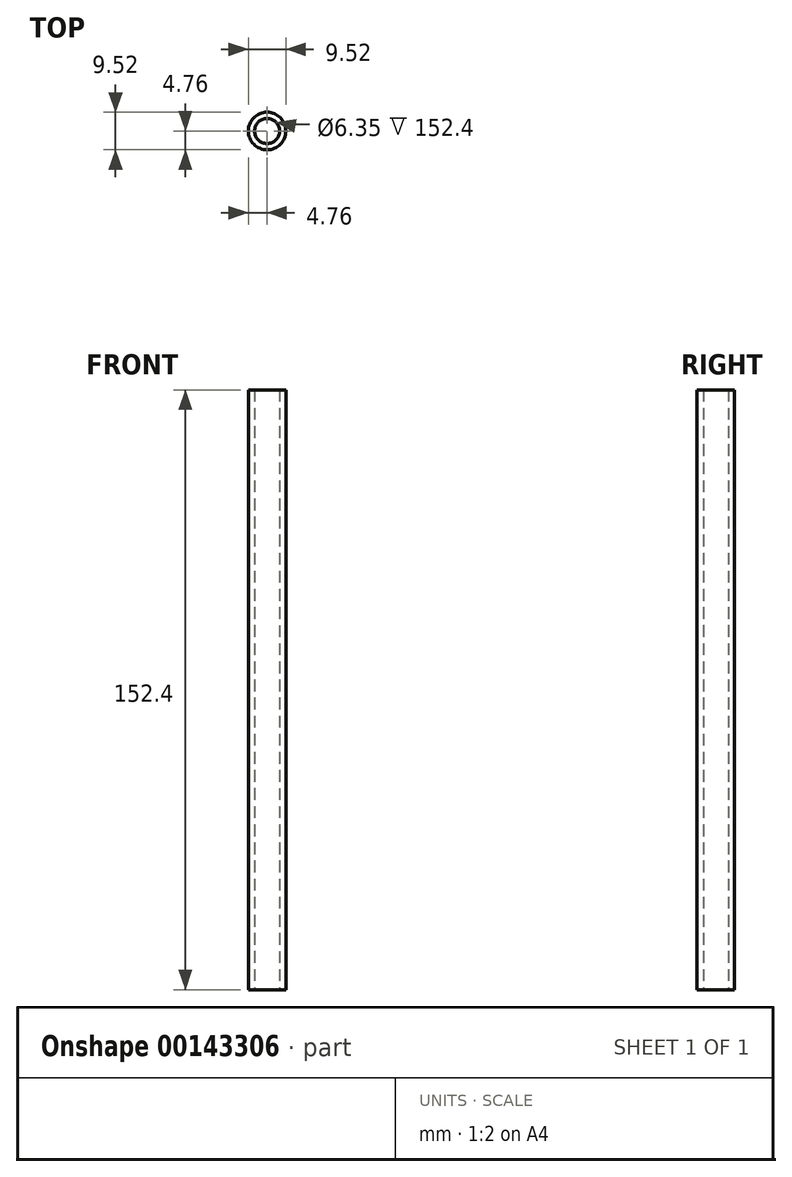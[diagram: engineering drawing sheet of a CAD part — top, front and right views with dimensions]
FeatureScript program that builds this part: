
annotation { "Feature Type Name" : "Feature", "Feature Type Description" : "" }
export const myFeature = defineFeature(function(context is Context, id is Id, definition is map)
    precondition{}
    {
        {
            var Q0;
            Q0=qCreatedBy(makeId("Top.planeOp"),FACE);
            var sketch = newSketch(context, id + "F0", { "sketchPlane" : qUnion([Q0])});
            skCircle(sketch, "E0", {"center": v(0, 0) * mm, "radius": 4.76 * mm});
            skCircle(sketch, "E1", {"center": v(0, 0) * mm, "radius": 3.18 * mm});
            skSolve(sketch);
        }
        {
            var Q0;
            Q0 = qSketchRegion(id + "F0", true);
            extrude(context, id + "F1", {"entities" : qUnion([Q0]), "depth" : 152.4 * mm, "offsetDistance" : 25.4 * mm});
        }
    });
